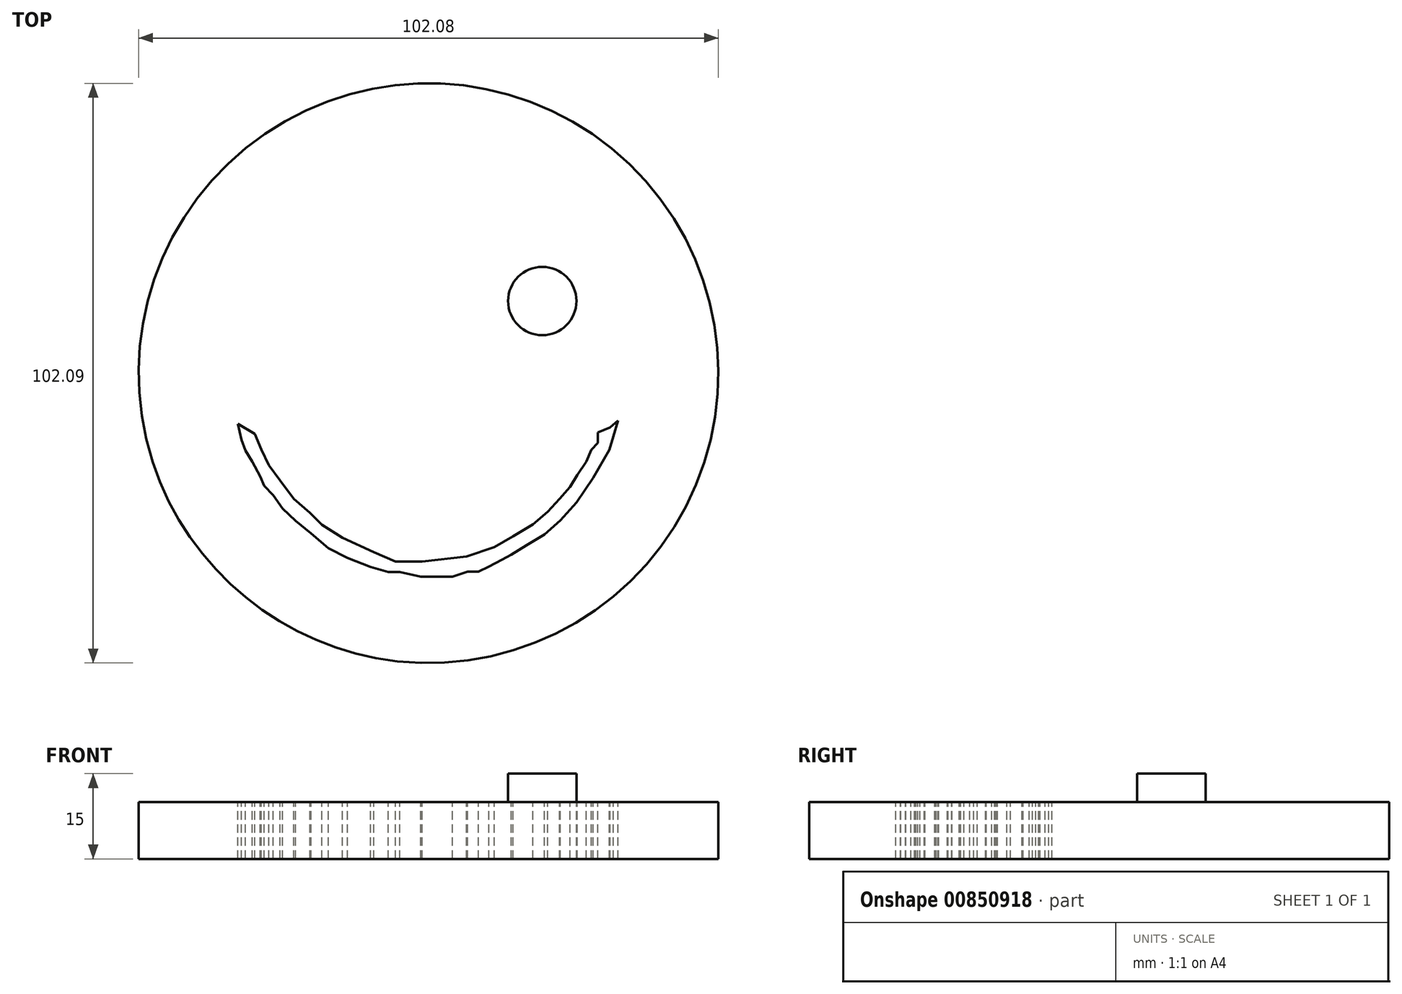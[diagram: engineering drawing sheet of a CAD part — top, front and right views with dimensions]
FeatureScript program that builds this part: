
annotation { "Feature Type Name" : "Feature", "Feature Type Description" : "" }
export const myFeature = defineFeature(function(context is Context, id is Id, definition is map)
    precondition{}
    {
        {
            var Q0;
            Q0=qCreatedBy(makeId("Top.planeOp"),FACE);
            var sketch = newSketch(context, id + "F0", { "sketchPlane" : qUnion([Q0])});
            skCircle(sketch, "E0", {"center": v(3.16, -22.76) * mm, "radius": 51.04 * mm});
            skSolve(sketch);
        }
        {
            var Q0;
            Q0=makeQuery(id+"F0.imprint","IMPRINT",FACE,{"disambiguationData":[TD([[makeQuery(id+"F0.imprint","IMPRINT",EDGE,{"derivedFrom":sQuery(id+"F0.wireOp",EDGE,"E0")}),1.0]])]});
            var sketch = newSketch(context, id + "F1", { "sketchPlane" : qUnion([Q0])});
            skCircle(sketch, "E1", {"center": v(3.6, -22.23) * mm, "radius": 51.62 * mm});
            skPoint(sketch, "E1.first.point", {"position": v(-18.43, 24.46) * mm});
            skPoint(sketch, "E1.second.point", {"position": v(55.07, -26.08) * mm});
            skPoint(sketch, "E1.third.point", {"position": v(-35.04, -56.47) * mm});
            skSolve(sketch);
        }
        {
            var Q0;
            {var subQ0=sQuery(id+"F1.wireOp",EDGE,"E1");var subQ1=makeQuery(id+"F0.imprint","IMPRINT",EDGE,{"derivedFrom":sQuery(id+"F0.wireOp",EDGE,"E0")});var subQ2=makeQuery(id+"F1.imprint","INTERSECT",VERTEX,{"disambiguationData":[OD(0.0)],"derivedFrom":[subQ1,subQ0]});Q0=makeQuery(id+"F1.imprint","IMPRINT",FACE,{"disambiguationData":[TD([[makeQuery(id+"F1.imprint","IMPRINT",EDGE,{"disambiguationData":[TD([[subQ2,-1.0]])],"derivedFrom":subQ0}),1.0]])]});}
            extrude(context, id + "F2", {"entities" : qUnion([Q0]), "depth" : 10 * mm, "offsetDistance" : 25 * mm});
        }
        {
            var Q0;
            Q0=makeQuery(id+"F2.opExtrude","CAP_FACE",FACE,{"disambiguationData":[OSD([sQuery(id+"F0.wireOp",EDGE,"E0"),sQuery(id+"F1.wireOp",EDGE,"E1")])],"isStart":false});
            var sketch = newSketch(context, id + "F3", { "sketchPlane" : qUnion([Q0])});
            skCircle(sketch, "E2", {"center": v(23.18, -10.07) * mm, "radius": 6.02 * mm});
            skPoint(sketch, "E2.first.point", {"position": v(23.32, -4.05) * mm});
            skPoint(sketch, "E2.second.point", {"position": v(28.76, -12.32) * mm});
            skPoint(sketch, "E2.third.point", {"position": v(18.5, -13.84) * mm});
            skSolve(sketch);
        }
        {
            var Q0;
            Q0 = qSketchRegion(id + "F3", true);
            extrude(context, id + "F4", {"entities" : qUnion([Q0]), "operationType" : NewBodyOperationType.ADD, "depth" : 5 * mm, "offsetDistance" : 25 * mm});
        }
        {
            var Q0;
            Q0=makeQuery(id+"F2.opExtrude","CAP_FACE",FACE,{"disambiguationData":[OSD([sQuery(id+"F0.wireOp",EDGE,"E0"),sQuery(id+"F1.wireOp",EDGE,"E1")])],"isStart":false});
            var sketch = newSketch(context, id + "F5", { "sketchPlane" : qUnion([Q0])});
            skCircle(sketch, "E3", {"center": v(-19.22, -10.42) * mm, "radius": 6.41 * mm});
            skPoint(sketch, "E3.first.point", {"position": v(-19.07, -4.01) * mm});
            skPoint(sketch, "E3.second.point", {"position": v(-13.4, -13.13) * mm});
            skPoint(sketch, "E3.third.point", {"position": v(-24.44, -14.14) * mm});
            skSolve(sketch);
        }
        {
            var Q0;
            Q0=sQuery(id+"F5.wireOp",EDGE,"E3");
            extrude(context, id + "F6", {"bodyType" : ToolBodyType.SURFACE, "surfaceEntities" : qUnion([Q0]), "depth" : 5 * mm, "offsetDistance" : 25 * mm});
        }
        {
            var Q0;
            Q0=makeQuery(id+"F2.opExtrude","CAP_FACE",FACE,{"disambiguationData":[OSD([sQuery(id+"F0.wireOp",EDGE,"E0"),sQuery(id+"F1.wireOp",EDGE,"E1")])],"isStart":false});
            var sketch = newSketch(context, id + "F7", { "sketchPlane" : qUnion([Q0])});
            skLineSegment(sketch, "E4", {"start": v(-30.42, -31.69) * mm, "end": v(-29.77, -34.5) * mm});
            skLineSegment(sketch, "E5", {"start": v(-29.77, -34.5) * mm, "end": v(-29.05, -36.36) * mm});
            skLineSegment(sketch, "E6", {"start": v(-29.05, -36.36) * mm, "end": v(-27.84, -38.37) * mm});
            skLineSegment(sketch, "E7", {"start": v(-27.84, -38.37) * mm, "end": v(-26.47, -40.95) * mm});
            skLineSegment(sketch, "E8", {"start": v(-26.47, -40.95) * mm, "end": v(-25.75, -42.64) * mm});
            skLineSegment(sketch, "E9", {"start": v(-25.75, -42.64) * mm, "end": v(-24.21, -44.25) * mm});
            skLineSegment(sketch, "E10", {"start": v(-24.21, -44.25) * mm, "end": v(-22.52, -46.59) * mm});
            skLineSegment(sketch, "E11", {"start": v(-22.52, -46.59) * mm, "end": v(-20.27, -48.76) * mm});
            skLineSegment(sketch, "E12", {"start": v(-20.27, -48.76) * mm, "end": v(-17.53, -51.02) * mm});
            skLineSegment(sketch, "E13", {"start": v(-17.53, -51.02) * mm, "end": v(-14.47, -53.6) * mm});
            skLineSegment(sketch, "E14", {"start": v(-14.47, -53.6) * mm, "end": v(-11.09, -55.29) * mm});
            skLineSegment(sketch, "E15", {"start": v(-11.09, -55.29) * mm, "end": v(-7.06, -56.9) * mm});
            skLineSegment(sketch, "E16", {"start": v(-7.06, -56.9) * mm, "end": v(-3.92, -57.79) * mm});
            skLineSegment(sketch, "E17", {"start": v(-3.92, -57.79) * mm, "end": v(-1.9, -57.79) * mm});
            skLineSegment(sketch, "E18", {"start": v(-1.9, -57.79) * mm, "end": v(1.8, -58.6) * mm});
            skLineSegment(sketch, "E19", {"start": v(1.8, -58.6) * mm, "end": v(5.67, -58.6) * mm});
            skLineSegment(sketch, "E20", {"start": v(5.67, -58.6) * mm, "end": v(7.36, -58.6) * mm});
            skLineSegment(sketch, "E21", {"start": v(7.36, -58.6) * mm, "end": v(10.02, -57.7) * mm});
            skLineSegment(sketch, "E22", {"start": v(10.02, -57.7) * mm, "end": v(11.95, -57.7) * mm});
            skLineSegment(sketch, "E23", {"start": v(11.95, -57.7) * mm, "end": v(13.8, -56.82) * mm});
            skLineSegment(sketch, "E24", {"start": v(13.8, -56.82) * mm, "end": v(16.06, -55.61) * mm});
            skLineSegment(sketch, "E25", {"start": v(16.06, -55.61) * mm, "end": v(17.75, -54.73) * mm});
            skLineSegment(sketch, "E26", {"start": v(17.75, -54.73) * mm, "end": v(20.4, -53.11) * mm});
            skLineSegment(sketch, "E27", {"start": v(20.4, -53.11) * mm, "end": v(23.55, -51.18) * mm});
            skLineSegment(sketch, "E28", {"start": v(23.55, -51.18) * mm, "end": v(26.37, -48.68) * mm});
            skLineSegment(sketch, "E29", {"start": v(26.37, -48.68) * mm, "end": v(29.19, -45.54) * mm});
            skLineSegment(sketch, "E30", {"start": v(29.19, -45.54) * mm, "end": v(32.17, -41.2) * mm});
            skLineSegment(sketch, "E31", {"start": v(32.17, -41.2) * mm, "end": v(34.99, -36.28) * mm});
            skLineSegment(sketch, "E32", {"start": v(34.99, -36.28) * mm, "end": v(35.71, -33.94) * mm});
            skLineSegment(sketch, "E33", {"start": v(35.71, -33.94) * mm, "end": v(36.52, -31.12) * mm});
            skLineSegment(sketch, "E34", {"start": v(36.52, -31.12) * mm, "end": v(35.15, -32.33) * mm});
            skLineSegment(sketch, "E35", {"start": v(35.15, -32.33) * mm, "end": v(32.97, -33.22) * mm});
            skLineSegment(sketch, "E36", {"start": v(32.97, -33.22) * mm, "end": v(32.97, -35.07) * mm});
            skLineSegment(sketch, "E37", {"start": v(32.97, -35.07) * mm, "end": v(31.85, -36.28) * mm});
            skLineSegment(sketch, "E38", {"start": v(31.85, -36.28) * mm, "end": v(30.96, -38.37) * mm});
            skLineSegment(sketch, "E39", {"start": v(30.96, -38.37) * mm, "end": v(29.35, -40.7) * mm});
            skLineSegment(sketch, "E40", {"start": v(29.35, -40.7) * mm, "end": v(28.06, -42.8) * mm});
            skLineSegment(sketch, "E41", {"start": v(28.06, -42.8) * mm, "end": v(26.2, -44.9) * mm});
            skLineSegment(sketch, "E42", {"start": v(26.2, -44.9) * mm, "end": v(24.11, -47.15) * mm});
            skLineSegment(sketch, "E43", {"start": v(24.11, -47.15) * mm, "end": v(21.54, -49.4) * mm});
            skLineSegment(sketch, "E44", {"start": v(21.54, -49.4) * mm, "end": v(18.07, -51.5) * mm});
            skLineSegment(sketch, "E45", {"start": v(18.07, -51.5) * mm, "end": v(14.77, -53.44) * mm});
            skLineSegment(sketch, "E46", {"start": v(14.77, -53.44) * mm, "end": v(9.86, -55.05) * mm});
            skLineSegment(sketch, "E47", {"start": v(9.86, -55.05) * mm, "end": v(2.04, -55.93) * mm});
            skLineSegment(sketch, "E48", {"start": v(2.04, -55.93) * mm, "end": v(-2.63, -55.93) * mm});
            skLineSegment(sketch, "E49", {"start": v(-2.63, -55.93) * mm, "end": v(-6.5, -54.32) * mm});
            skLineSegment(sketch, "E50", {"start": v(-6.5, -54.32) * mm, "end": v(-11.97, -51.74) * mm});
            skLineSegment(sketch, "E51", {"start": v(-11.97, -51.74) * mm, "end": v(-15.6, -49.49) * mm});
            skLineSegment(sketch, "E52", {"start": v(-15.6, -49.49) * mm, "end": v(-17.7, -47.4) * mm});
            skLineSegment(sketch, "E53", {"start": v(-17.7, -47.4) * mm, "end": v(-20.6, -44.9) * mm});
            skLineSegment(sketch, "E54", {"start": v(-20.6, -44.9) * mm, "end": v(-23, -41.68) * mm});
            skLineSegment(sketch, "E55", {"start": v(-23, -41.68) * mm, "end": v(-24.94, -39.02) * mm});
            skLineSegment(sketch, "E56", {"start": v(-24.94, -39.02) * mm, "end": v(-26.3, -36.2) * mm});
            skLineSegment(sketch, "E57", {"start": v(-26.3, -36.2) * mm, "end": v(-27.44, -33.46) * mm});
            skLineSegment(sketch, "E58", {"start": v(-27.44, -33.46) * mm, "end": v(-30.42, -31.69) * mm});
            skSolve(sketch);
        }
        {
            var Q0;
            Q0=makeQuery(id+"FkvOfJxCabjrfWA_2.opExtrude","CAP_FACE",FACE,{"disambiguationData":[OSD([sQuery(id+"F7.wireOp",EDGE,"E4"),sQuery(id+"F7.wireOp",EDGE,"E5"),sQuery(id+"F7.wireOp",EDGE,"E6"),sQuery(id+"F7.wireOp",EDGE,"E7"),sQuery(id+"F7.wireOp",EDGE,"E8"),sQuery(id+"F7.wireOp",EDGE,"E9"),sQuery(id+"F7.wireOp",EDGE,"E10"),sQuery(id+"F7.wireOp",EDGE,"E11"),sQuery(id+"F7.wireOp",EDGE,"E12"),sQuery(id+"F7.wireOp",EDGE,"E13"),sQuery(id+"F7.wireOp",EDGE,"E14"),sQuery(id+"F7.wireOp",EDGE,"E15"),sQuery(id+"F7.wireOp",EDGE,"E16"),sQuery(id+"F7.wireOp",EDGE,"E17"),sQuery(id+"F7.wireOp",EDGE,"E18"),sQuery(id+"F7.wireOp",EDGE,"E19"),sQuery(id+"F7.wireOp",EDGE,"E20"),sQuery(id+"F7.wireOp",EDGE,"E21"),sQuery(id+"F7.wireOp",EDGE,"E22"),sQuery(id+"F7.wireOp",EDGE,"E23"),sQuery(id+"F7.wireOp",EDGE,"E24"),sQuery(id+"F7.wireOp",EDGE,"E25"),sQuery(id+"F7.wireOp",EDGE,"E26"),sQuery(id+"F7.wireOp",EDGE,"E27"),sQuery(id+"F7.wireOp",EDGE,"E28"),sQuery(id+"F7.wireOp",EDGE,"E29"),sQuery(id+"F7.wireOp",EDGE,"E30"),sQuery(id+"F7.wireOp",EDGE,"E31"),sQuery(id+"F7.wireOp",EDGE,"E32"),sQuery(id+"F7.wireOp",EDGE,"E33"),sQuery(id+"F7.wireOp",EDGE,"E34"),sQuery(id+"F7.wireOp",EDGE,"E35"),sQuery(id+"F7.wireOp",EDGE,"E36"),sQuery(id+"F7.wireOp",EDGE,"E37"),sQuery(id+"F7.wireOp",EDGE,"E38"),sQuery(id+"F7.wireOp",EDGE,"E39"),sQuery(id+"F7.wireOp",EDGE,"E40"),sQuery(id+"F7.wireOp",EDGE,"E41"),sQuery(id+"F7.wireOp",EDGE,"E42"),sQuery(id+"F7.wireOp",EDGE,"E43"),sQuery(id+"F7.wireOp",EDGE,"E44"),sQuery(id+"F7.wireOp",EDGE,"E45"),sQuery(id+"F7.wireOp",EDGE,"E46"),sQuery(id+"F7.wireOp",EDGE,"E47"),sQuery(id+"F7.wireOp",EDGE,"E48"),sQuery(id+"F7.wireOp",EDGE,"E49"),sQuery(id+"F7.wireOp",EDGE,"E50"),sQuery(id+"F7.wireOp",EDGE,"E51"),sQuery(id+"F7.wireOp",EDGE,"E52"),sQuery(id+"F7.wireOp",EDGE,"E53"),sQuery(id+"F7.wireOp",EDGE,"E54"),sQuery(id+"F7.wireOp",EDGE,"E55"),sQuery(id+"F7.wireOp",EDGE,"E56"),sQuery(id+"F7.wireOp",EDGE,"E57"),sQuery(id+"F7.wireOp",EDGE,"E58")])],"isStart":false});
            var sketch = newSketch(context, id + "F8", { "sketchPlane" : qUnion([Q0])});
            skSolve(sketch);
        }
        {
            var Q0;
            Q0 = qSketchRegion(id + "F7", true);
            var Q1;
            Q1=makeQuery(id+"FkvOfJxCabjrfWA_2.opExtrude","SWEPT_FACE",FACE,{"disambiguationData":[OSD([sQuery(id+"F7.wireOp",EDGE,"E30")])]});
            var Q2;
            Q2=makeQuery(id+"F8.imprint","IMPRINT",FACE,{"disambiguationData":[TD([[makeQuery(id+"F8.imprint","IMPRINT",EDGE,{"derivedFrom":makeQuery(id+"FkvOfJxCabjrfWA_2.opExtrude","CAP_EDGE",EDGE,{"disambiguationData":[OSD([sQuery(id+"F7.wireOp",EDGE,"E4")])],"isStart":false})}),1.0]])]});
            extrude(context, id + "F9", {"entities" : qUnion([Q0, Q1, Q2]), "endBound" : BoundingType.UP_TO_NEXT, "oppositeDirection" : true, "depth" : 13.7 * mm, "offsetDistance" : 25 * mm});
        }
        {
            var Q0;
            Q0=makeQuery(id+"F9.opExtrude","CAP_FACE",FACE,{"disambiguationData":[OSD([sQuery(id+"F7.wireOp",EDGE,"E4"),sQuery(id+"F7.wireOp",EDGE,"E5"),sQuery(id+"F7.wireOp",EDGE,"E6"),sQuery(id+"F7.wireOp",EDGE,"E7"),sQuery(id+"F7.wireOp",EDGE,"E8"),sQuery(id+"F7.wireOp",EDGE,"E9"),sQuery(id+"F7.wireOp",EDGE,"E10"),sQuery(id+"F7.wireOp",EDGE,"E11"),sQuery(id+"F7.wireOp",EDGE,"E12"),sQuery(id+"F7.wireOp",EDGE,"E13"),sQuery(id+"F7.wireOp",EDGE,"E14"),sQuery(id+"F7.wireOp",EDGE,"E15"),sQuery(id+"F7.wireOp",EDGE,"E16"),sQuery(id+"F7.wireOp",EDGE,"E17"),sQuery(id+"F7.wireOp",EDGE,"E18"),sQuery(id+"F7.wireOp",EDGE,"E19"),sQuery(id+"F7.wireOp",EDGE,"E20"),sQuery(id+"F7.wireOp",EDGE,"E21"),sQuery(id+"F7.wireOp",EDGE,"E22"),sQuery(id+"F7.wireOp",EDGE,"E23"),sQuery(id+"F7.wireOp",EDGE,"E24"),sQuery(id+"F7.wireOp",EDGE,"E25"),sQuery(id+"F7.wireOp",EDGE,"E26"),sQuery(id+"F7.wireOp",EDGE,"E27"),sQuery(id+"F7.wireOp",EDGE,"E28"),sQuery(id+"F7.wireOp",EDGE,"E29"),sQuery(id+"F7.wireOp",EDGE,"E30"),sQuery(id+"F7.wireOp",EDGE,"E31"),sQuery(id+"F7.wireOp",EDGE,"E32"),sQuery(id+"F7.wireOp",EDGE,"E33"),sQuery(id+"F7.wireOp",EDGE,"E34"),sQuery(id+"F7.wireOp",EDGE,"E35"),sQuery(id+"F7.wireOp",EDGE,"E36"),sQuery(id+"F7.wireOp",EDGE,"E37"),sQuery(id+"F7.wireOp",EDGE,"E38"),sQuery(id+"F7.wireOp",EDGE,"E39"),sQuery(id+"F7.wireOp",EDGE,"E40"),sQuery(id+"F7.wireOp",EDGE,"E41"),sQuery(id+"F7.wireOp",EDGE,"E42"),sQuery(id+"F7.wireOp",EDGE,"E43"),sQuery(id+"F7.wireOp",EDGE,"E44"),sQuery(id+"F7.wireOp",EDGE,"E45"),sQuery(id+"F7.wireOp",EDGE,"E46"),sQuery(id+"F7.wireOp",EDGE,"E47"),sQuery(id+"F7.wireOp",EDGE,"E48"),sQuery(id+"F7.wireOp",EDGE,"E49"),sQuery(id+"F7.wireOp",EDGE,"E50"),sQuery(id+"F7.wireOp",EDGE,"E51"),sQuery(id+"F7.wireOp",EDGE,"E52"),sQuery(id+"F7.wireOp",EDGE,"E53"),sQuery(id+"F7.wireOp",EDGE,"E54"),sQuery(id+"F7.wireOp",EDGE,"E55"),sQuery(id+"F7.wireOp",EDGE,"E56"),sQuery(id+"F7.wireOp",EDGE,"E57"),sQuery(id+"F7.wireOp",EDGE,"E58")])],"isStart":true});
            extrude(context, id + "F10", {"entities" : qUnion([Q0]), "endBound" : BoundingType.UP_TO_NEXT, "oppositeDirection" : true, "depth" : 25 * mm, "offsetDistance" : 25 * mm});
        }
    });
